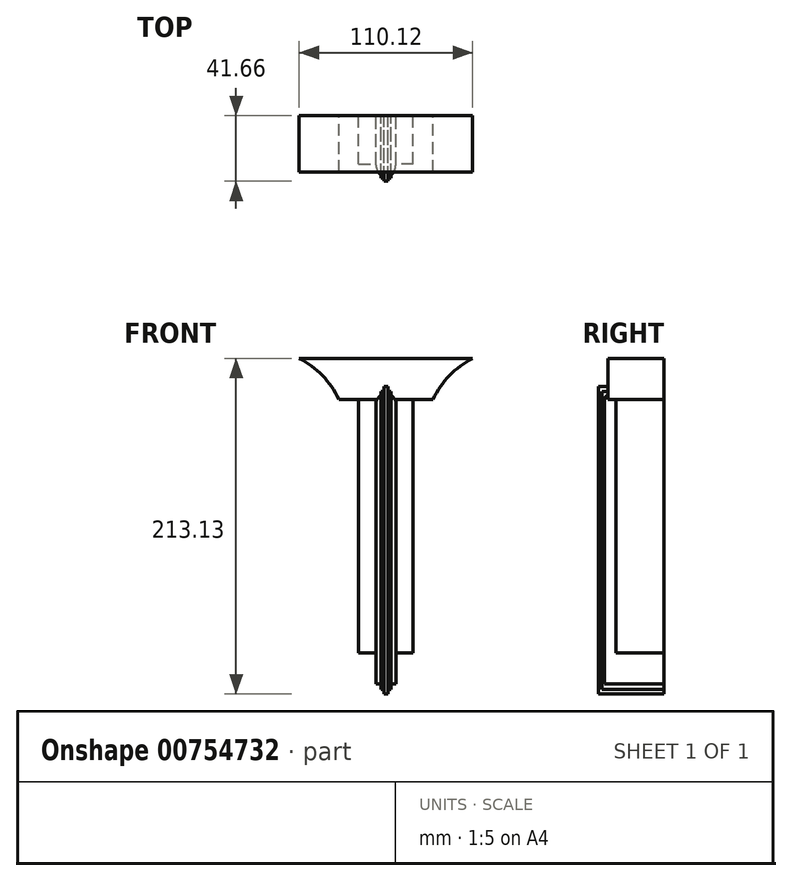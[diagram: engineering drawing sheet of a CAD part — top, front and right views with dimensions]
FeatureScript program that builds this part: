
annotation { "Feature Type Name" : "Feature", "Feature Type Description" : "" }
export const myFeature = defineFeature(function(context is Context, id is Id, definition is map)
    precondition{}
    {
        {
            var Q0;
            Q0=qCreatedBy(makeId("Front.planeOp"),FACE);
            var sketch = newSketch(context, id + "F0", { "sketchPlane" : qUnion([Q0])});
            skLineSegment(sketch, "E0", {"start": v(-55.06, 36.57) * mm, "end": v(0, 36.57) * mm});
            skLineSegment(sketch, "E1", {"start": v(-29.96, 10.57) * mm, "end": v(-17.33, 10.57) * mm});
            skLineSegment(sketch, "E2", {"start": v(-17.33, 10.57) * mm, "end": v(-17.33, -150.47) * mm});
            skLineSegment(sketch, "E3", {"start": v(-17.33, -150.47) * mm, "end": v(-6.23, -150.47) * mm});
            skLineSegment(sketch, "E4", {"start": v(-6.23, -150.47) * mm, "end": v(-6.23, -170.3) * mm});
            skPoint(sketch, "E5.start.orphan", {"position": v(-3.11, -170.3) * mm});
            skLineSegment(sketch, "E6", {"start": v(-17.33, 10.57) * mm, "end": v(-6.23, 10.57) * mm});
            skLineSegment(sketch, "E7", {"start": v(-6.23, -150.47) * mm, "end": v(-6.23, 10.57) * mm});
            skLineSegment(sketch, "E8.MirrorCS", {"start": v(55.06, 36.57) * mm, "end": v(0, 36.57) * mm});
            skLineSegment(sketch, "E9.MirrorCS", {"start": v(29.96, 10.57) * mm, "end": v(17.33, 10.57) * mm});
            skLineSegment(sketch, "E10.MirrorCS", {"start": v(17.33, 10.57) * mm, "end": v(6.23, 10.57) * mm});
            skLineSegment(sketch, "E11.MirrorCS", {"start": v(3.11, -170.3) * mm, "end": v(3.11, 10.57) * mm});
            skLineSegment(sketch, "E12.MirrorCS", {"start": v(6.23, -150.47) * mm, "end": v(6.23, 10.57) * mm});
            skLineSegment(sketch, "E13.MirrorCS", {"start": v(17.33, 10.57) * mm, "end": v(17.33, -150.47) * mm});
            skLineSegment(sketch, "E14.MirrorCS", {"start": v(6.23, -150.47) * mm, "end": v(6.23, -170.3) * mm});
            skLineSegment(sketch, "E15.MirrorCS", {"start": v(17.33, -150.47) * mm, "end": v(6.23, -150.47) * mm});
            skPoint(sketch, "E16.orphan", {"position": v(0, -170.3) * mm});
            skPoint(sketch, "E17.MirrorCS.start.orphan", {"position": v(6.23, -170.3) * mm});
            skLineSegment(sketch, "E18", {"start": v(-3.11, 10.57) * mm, "end": v(-3.11, -173.81) * mm});
            skLineSegment(sketch, "E19", {"start": v(-3.11, -173.81) * mm, "end": v(-1.38, -173.81) * mm});
            skLineSegment(sketch, "E20", {"start": v(-1.38, -173.81) * mm, "end": v(-1.38, -176.56) * mm});
            skLineSegment(sketch, "E21", {"start": v(-1.38, -176.56) * mm, "end": v(0, -176.56) * mm});
            skLineSegment(sketch, "E22", {"start": v(-6.23, -170.3) * mm, "end": v(-3.11, -170.3) * mm});
            skLineSegment(sketch, "E23", {"start": v(-1.38, -173.81) * mm, "end": v(-1.38, 10.57) * mm});
            skLineSegment(sketch, "E24.MirrorCS", {"start": v(1.38, -173.81) * mm, "end": v(1.38, 10.57) * mm});
            skLineSegment(sketch, "E25.MirrorCS", {"start": v(1.38, -176.56) * mm, "end": v(0, -176.56) * mm});
            skLineSegment(sketch, "E26.MirrorCS", {"start": v(1.38, -173.81) * mm, "end": v(1.38, -176.56) * mm});
            skLineSegment(sketch, "E27.MirrorCS", {"start": v(3.11, -173.81) * mm, "end": v(1.38, -173.81) * mm});
            skLineSegment(sketch, "E28.MirrorCS", {"start": v(3.11, 10.57) * mm, "end": v(3.11, -173.81) * mm});
            skLineSegment(sketch, "E29.MirrorCS", {"start": v(6.23, -170.3) * mm, "end": v(3.11, -170.3) * mm});
            skPoint(sketch, "E30.MirrorCS.end.orphan", {"position": v(55.06, 36.57) * mm});
            skPoint(sketch, "E30.MirrorCS.start.orphan", {"position": v(29.96, 10.57) * mm});
            skArc(sketch, "E31", {"start": v(-29.96, 10.57) * mm, "mid": v(-40.39, 25.61) * mm, "end": v(-55.06, 36.57) * mm});
            skArc(sketch, "E32.MirrorCS", {"start": v(29.96, 10.57) * mm, "mid": v(40.39, 25.61) * mm, "end": v(55.06, 36.57) * mm});
            skLineSegment(sketch, "E33", {"start": v(-6.23, 10.57) * mm, "end": v(-6.23, 13.54) * mm});
            skLineSegment(sketch, "E34", {"start": v(-6.23, 13.54) * mm, "end": v(-3.11, 13.54) * mm});
            skLineSegment(sketch, "E35", {"start": v(-3.11, 10.57) * mm, "end": v(-3.11, 13.54) * mm});
            skLineSegment(sketch, "E36", {"start": v(3.11, 13.54) * mm, "end": v(6.23, 13.54) * mm});
            skLineSegment(sketch, "E37", {"start": v(6.23, 10.57) * mm, "end": v(6.23, 13.54) * mm});
            skLineSegment(sketch, "E38", {"start": v(3.11, 10.57) * mm, "end": v(3.11, 15.38) * mm});
            skLineSegment(sketch, "E39", {"start": v(3.11, 15.38) * mm, "end": v(1.35, 15.38) * mm});
            skLineSegment(sketch, "E40", {"start": v(1.38, 10.57) * mm, "end": v(1.38, 15.38) * mm});
            skLineSegment(sketch, "E41", {"start": v(-1.38, 10.57) * mm, "end": v(-1.38, 15.38) * mm});
            skLineSegment(sketch, "E42", {"start": v(-1.38, 15.38) * mm, "end": v(-3.11, 15.38) * mm});
            skLineSegment(sketch, "E43", {"start": v(-3.11, 13.54) * mm, "end": v(-3.11, 15.38) * mm});
            skLineSegment(sketch, "E44", {"start": v(-1.38, 15.38) * mm, "end": v(-1.38, 18.81) * mm});
            skLineSegment(sketch, "E45", {"start": v(-1.38, 18.81) * mm, "end": v(0, 18.81) * mm});
            skLineSegment(sketch, "E46.MirrorCS", {"start": v(1.38, 18.81) * mm, "end": v(0, 18.81) * mm});
            skLineSegment(sketch, "E47.MirrorCS", {"start": v(1.38, 15.38) * mm, "end": v(1.38, 18.81) * mm});
            skSolve(sketch);
        }
        {
            var Q0;
            Q0=makeQuery(id+"F0.imprint","IMPRINT",FACE,{"disambiguationData":[TD([[makeQuery(id+"F0.imprint","IMPRINT",EDGE,{"derivedFrom":sQuery(id+"F0.wireOp",EDGE,"E0")}),-1.0]])]});
            extrude(context, id + "F1", {"entities" : qUnion([Q0]), "depth" : 35.81 * mm, "offsetDistance" : 25.4 * mm});
        }
        {
            var Q0;
            {var subQ0=sQuery(id+"F0.wireOp",EDGE,"E2");Q0=makeQuery(id+"F0.imprint","IMPRINT",FACE,{"disambiguationData":[TD([[makeQuery(id+"F0.imprint","IMPRINT",EDGE,{"derivedFrom":subQ0}),1.0]])]});}
            extrude(context, id + "F2", {"entities" : qUnion([Q0]), "operationType" : NewBodyOperationType.ADD, "depth" : 30.73 * mm, "offsetDistance" : 25.4 * mm});
        }
        {
            var Q0;
            {var subQ2=sQuery(id+"F0.wireOp",EDGE,"E12.MirrorCS");Q0=makeQuery(id+"F0.imprint","IMPRINT",FACE,{"disambiguationData":[TD([[makeQuery(id+"F0.imprint","IMPRINT",EDGE,{"derivedFrom":subQ2}),-1.0]])]});}
            extrude(context, id + "F3", {"entities" : qUnion([Q0]), "operationType" : NewBodyOperationType.ADD, "depth" : 30.73 * mm, "offsetDistance" : 25.4 * mm});
        }
        {
            var Q0;
            Q0=makeQuery(id+"F0.imprint","IMPRINT",FACE,{"disambiguationData":[TD([[makeQuery(id+"F0.imprint","IMPRINT",EDGE,{"derivedFrom":sQuery(id+"F0.wireOp",EDGE,"E20")}),1.0]])]});
            extrude(context, id + "F4", {"entities" : qUnion([Q0]), "operationType" : NewBodyOperationType.ADD, "depth" : 41.66 * mm, "offsetDistance" : 25.4 * mm});
        }
        {
            var Q0;
            {var subQ0=sQuery(id+"F0.wireOp",EDGE,"E19");Q0=makeQuery(id+"F0.imprint","IMPRINT",FACE,{"disambiguationData":[TD([[makeQuery(id+"F0.imprint","IMPRINT",EDGE,{"derivedFrom":subQ0}),1.0]])]});}
            extrude(context, id + "F5", {"entities" : qUnion([Q0]), "operationType" : NewBodyOperationType.ADD, "depth" : 39.62 * mm, "offsetDistance" : 25.4 * mm});
        }
        {
            var Q0;
            Q0=makeQuery(id+"F0.imprint","IMPRINT",FACE,{"disambiguationData":[TD([[makeQuery(id+"F0.imprint","IMPRINT",EDGE,{"derivedFrom":sQuery(id+"F0.wireOp",EDGE,"E4")}),1.0]])]});
            extrude(context, id + "F6", {"entities" : qUnion([Q0]), "operationType" : NewBodyOperationType.ADD, "depth" : 37.85 * mm, "offsetDistance" : 25.4 * mm});
        }
        {
            var Q0;
            {var subQ5=sQuery(id+"F0.wireOp",EDGE,"E24.MirrorCS");Q0=makeQuery(id+"F0.imprint","IMPRINT",FACE,{"disambiguationData":[TD([[makeQuery(id+"F0.imprint","IMPRINT",EDGE,{"derivedFrom":subQ5}),-1.0]])]});}
            extrude(context, id + "F7", {"entities" : qUnion([Q0]), "operationType" : NewBodyOperationType.ADD, "depth" : 39.62 * mm, "offsetDistance" : 25.4 * mm});
        }
        {
            var Q0;
            {var subQ4=sQuery(id+"F0.wireOp",EDGE,"E12.MirrorCS");Q0=makeQuery(id+"F0.imprint","IMPRINT",FACE,{"disambiguationData":[TD([[makeQuery(id+"F0.imprint","IMPRINT",EDGE,{"derivedFrom":subQ4}),1.0]])]});}
            extrude(context, id + "F8", {"entities" : qUnion([Q0]), "operationType" : NewBodyOperationType.ADD, "depth" : 37.85 * mm, "offsetDistance" : 25.4 * mm});
        }
        {
            var Q0;
            Q0=makeQuery(id+"F6.opExtrude","CAP_EDGE",EDGE,{"disambiguationData":[OSD([sQuery(id+"F0.wireOp",EDGE,"E4"),sQuery(id+"F0.wireOp",EDGE,"E7")])],"isStart":false});
            fillet(context, id + "F9", {"entities" : qUnion([Q0]), "radius" : 7.97 * mm, "tangentPropagation" : true, "allowEdgeOverflow" : false});
        }
        {
            var Q0;
            Q0=makeQuery(id+"F8.opExtrude","CAP_EDGE",EDGE,{"disambiguationData":[OSD([sQuery(id+"F0.wireOp",EDGE,"E12.MirrorCS"),sQuery(id+"F0.wireOp",EDGE,"E14.MirrorCS")])],"isStart":false});
            fillet(context, id + "F10", {"entities" : qUnion([Q0]), "radius" : 7.98 * mm, "tangentPropagation" : true, "allowEdgeOverflow" : false});
        }
        {
            var Q0;
            Q0=makeQuery(id+"F10.opFillet","BLEND_EDGE",EDGE,{"blendedFrom":[makeQuery(id+"F8.opExtrude","CAP_EDGE",EDGE,{"disambiguationData":[OSD([sQuery(id+"F0.wireOp",EDGE,"E12.MirrorCS"),sQuery(id+"F0.wireOp",EDGE,"E14.MirrorCS"),sQuery(id+"F0.wireOp",EDGE,"E37")])],"isStart":false}),makeQuery(id+"F8.opExtrude","SWEPT_FACE",FACE,{"disambiguationData":[OSD([sQuery(id+"F0.wireOp",EDGE,"E36")])]})],"blendedInto":[makeQuery(id+"F8.opExtrude","SWEPT_FACE",FACE,{"disambiguationData":[OSD([sQuery(id+"F0.wireOp",EDGE,"E36")])]})]});
            fillet(context, id + "F11", {"entities" : qUnion([Q0]), "radius" : 2.97 * mm, "tangentPropagation" : true, "allowEdgeOverflow" : false});
        }
        {
            var Q0;
            Q0=makeQuery(id+"F9.opFillet","BLEND_EDGE",EDGE,{"blendedFrom":[makeQuery(id+"F6.opExtrude","CAP_EDGE",EDGE,{"disambiguationData":[OSD([sQuery(id+"F0.wireOp",EDGE,"E4"),sQuery(id+"F0.wireOp",EDGE,"E7"),sQuery(id+"F0.wireOp",EDGE,"E33")])],"isStart":false}),makeQuery(id+"F6.opExtrude","SWEPT_FACE",FACE,{"disambiguationData":[OSD([sQuery(id+"F0.wireOp",EDGE,"E34")])]})],"blendedInto":[makeQuery(id+"F6.opExtrude","SWEPT_FACE",FACE,{"disambiguationData":[OSD([sQuery(id+"F0.wireOp",EDGE,"E34")])]})]});
            fillet(context, id + "F12", {"entities" : qUnion([Q0]), "radius" : 2.97 * mm, "tangentPropagation" : true, "allowEdgeOverflow" : false});
        }
    });
